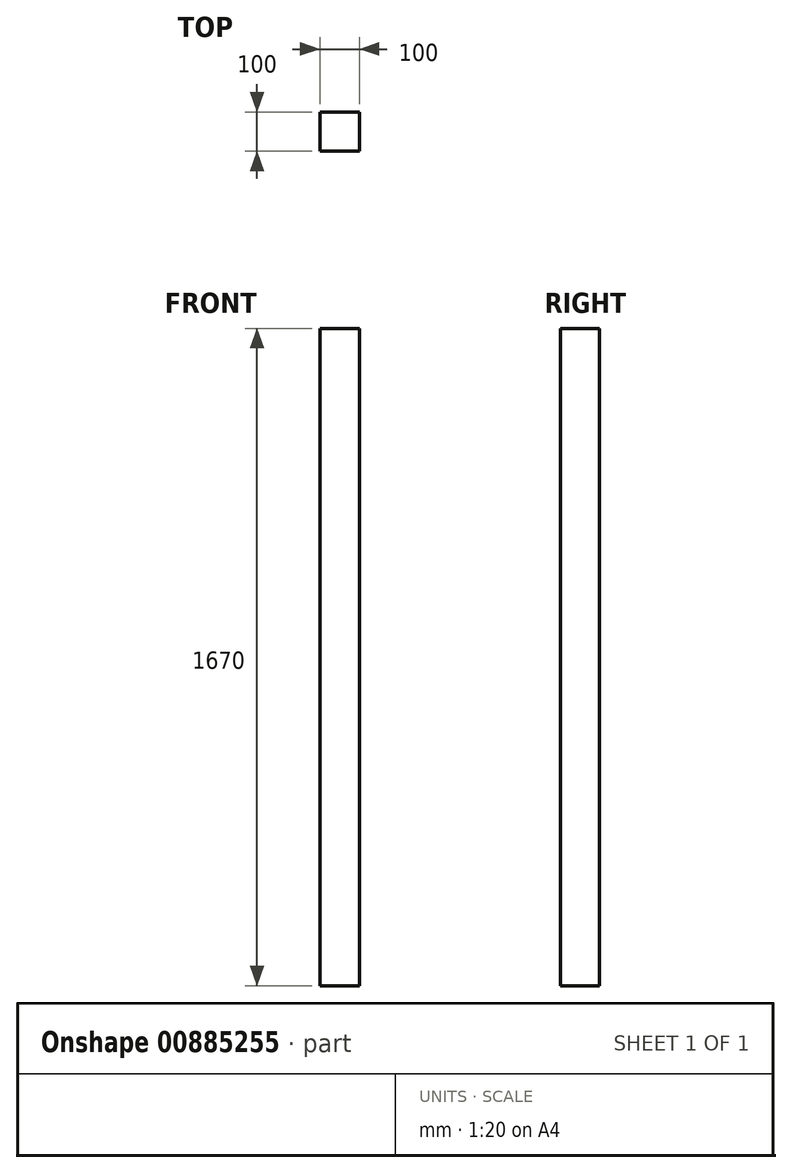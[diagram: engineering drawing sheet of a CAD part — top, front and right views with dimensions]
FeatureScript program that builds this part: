
annotation { "Feature Type Name" : "Feature", "Feature Type Description" : "" }
export const myFeature = defineFeature(function(context is Context, id is Id, definition is map)
    precondition{}
    {
        {
            var Q0;
            Q0=qCreatedBy(makeId("Top.planeOp"),FACE);
            var sketch = newSketch(context, id + "F0", { "sketchPlane" : qUnion([Q0])});
            skLineSegment(sketch, "E0.bottom", {"start": v(-50.07, 53.23) * mm, "end": v(49.93, 53.23) * mm});
            skLineSegment(sketch, "E0.top", {"start": v(-50.07, -46.77) * mm, "end": v(49.93, -46.77) * mm});
            skLineSegment(sketch, "E0.left", {"start": v(-50.07, 53.23) * mm, "end": v(-50.07, -46.77) * mm});
            skLineSegment(sketch, "E0.right", {"start": v(49.93, 53.23) * mm, "end": v(49.93, -46.77) * mm});
            skSolve(sketch);
        }
        {
            var Q0;
            Q0=makeQuery(id+"F0.imprint","IMPRINT",FACE,{"disambiguationData":[TD([[makeQuery(id+"F0.imprint","IMPRINT",EDGE,{"derivedFrom":sQuery(id+"F0.wireOp",EDGE,"E0.bottom")}),-1.0]])]});
            extrude(context, id + "F1", {"entities" : qUnion([Q0]), "depth" : 1670 * mm, "offsetDistance" : 25 * mm});
        }
    });
